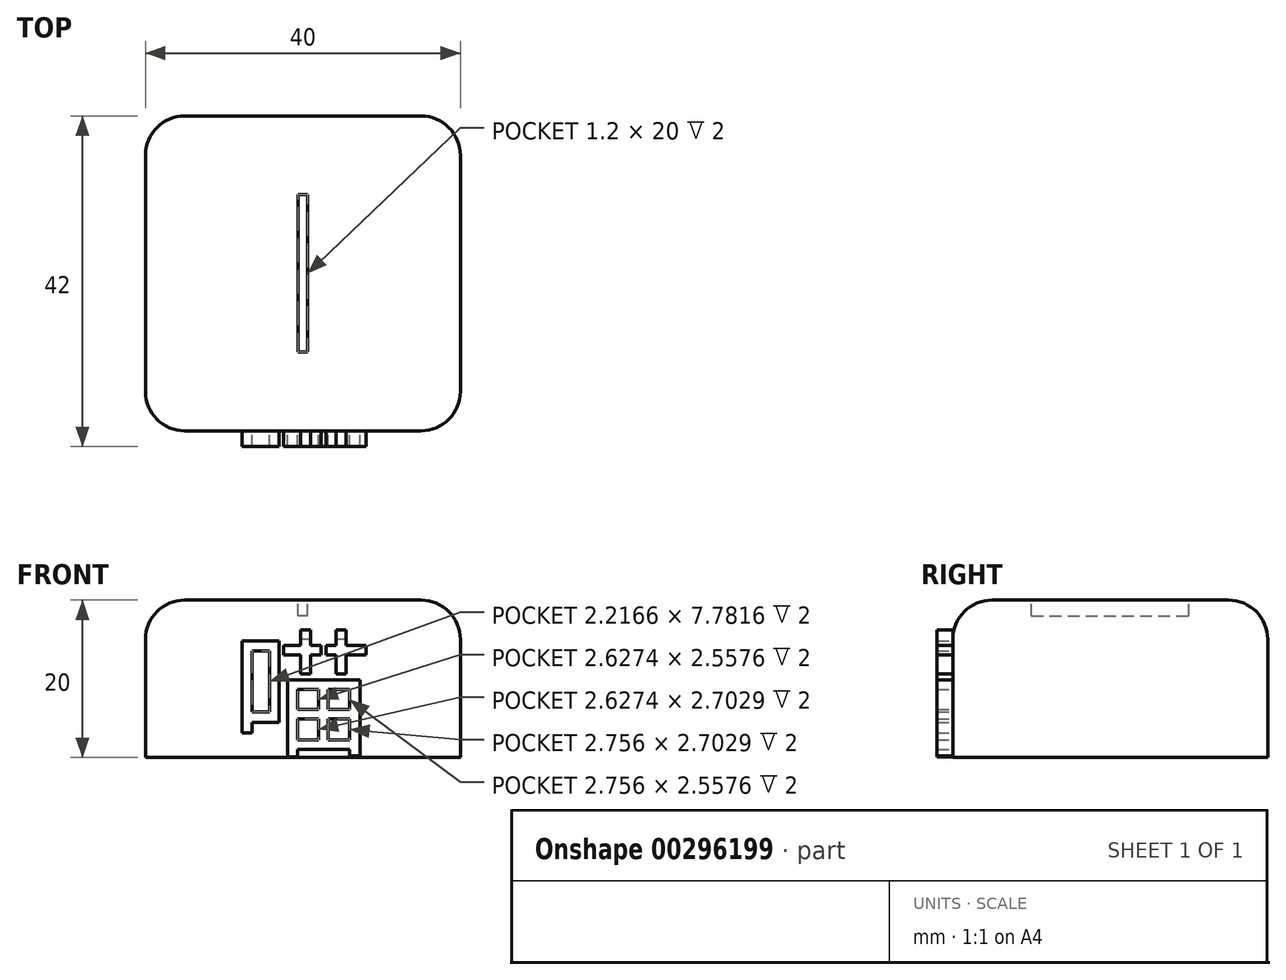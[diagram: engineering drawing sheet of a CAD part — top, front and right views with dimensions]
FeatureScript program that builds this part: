
annotation { "Feature Type Name" : "Feature", "Feature Type Description" : "" }
export const myFeature = defineFeature(function(context is Context, id is Id, definition is map)
    precondition{}
    {
        {
            var Q0;
            Q0=qCreatedBy(makeId("Top.planeOp"),FACE);
            var sketch = newSketch(context, id + "F0", { "sketchPlane" : qUnion([Q0])});
            skLineSegment(sketch, "E0.bottom", {"start": v(20, -20) * mm, "end": v(-20, -20) * mm});
            skLineSegment(sketch, "E0.top", {"start": v(20, 20) * mm, "end": v(-20, 20) * mm});
            skLineSegment(sketch, "E0.left", {"start": v(20, -20) * mm, "end": v(20, 20) * mm});
            skLineSegment(sketch, "E0.right", {"start": v(-20, -20) * mm, "end": v(-20, 20) * mm});
            skPoint(sketch, "E0.middle", {"position": v(0, 0) * mm});
            skLineSegment(sketch, "E1.bottom", {"start": v(0.6, -10) * mm, "end": v(-0.6, -10) * mm});
            skLineSegment(sketch, "E1.top", {"start": v(0.6, 10) * mm, "end": v(-0.6, 10) * mm});
            skLineSegment(sketch, "E1.left", {"start": v(0.6, -10) * mm, "end": v(0.6, 10) * mm});
            skLineSegment(sketch, "E1.right", {"start": v(-0.6, -10) * mm, "end": v(-0.6, 10) * mm});
            skSolve(sketch);
        }
        {
            var Q0;
            Q0=makeQuery(id+"F0.imprint","IMPRINT",FACE,{"disambiguationData":[TD([[makeQuery(id+"F0.imprint","IMPRINT",EDGE,{"derivedFrom":sQuery(id+"F0.wireOp",EDGE,"E0.bottom")}),-1.0]])]});
            var Q1;
            Q1=makeQuery(id+"F0.imprint","IMPRINT",FACE,{"disambiguationData":[TD([[makeQuery(id+"F0.imprint","IMPRINT",EDGE,{"derivedFrom":sQuery(id+"F0.wireOp",EDGE,"E1.bottom")}),-1.0]])]});
            extrude(context, id + "F1", {"entities" : qUnion([Q0, Q1]), "oppositeDirection" : true, "depth" : 20 * mm});
        }
        {
            var Q0;
            Q0=makeQuery(id+"F0.imprint","IMPRINT",FACE,{"disambiguationData":[TD([[makeQuery(id+"F0.imprint","IMPRINT",EDGE,{"derivedFrom":sQuery(id+"F0.wireOp",EDGE,"E1.bottom")}),-1.0]])]});
            extrude(context, id + "F2", {"entities" : qUnion([Q0]), "operationType" : NewBodyOperationType.REMOVE, "oppositeDirection" : true, "depth" : 2 * mm});
        }
        {
            var Q0;
            Q0=makeQuery(id+"F2.boolean.opBoolean","COPY",EDGE,{"derivedFrom":makeQuery(id+"F2.opExtrude","CAP_EDGE",EDGE,{"disambiguationData":[OSD([sQuery(id+"F0.wireOp",EDGE,"E1.left")])],"isStart":true})});
            var Q1;
            Q1=makeQuery(id+"F2.boolean.opBoolean","COPY",EDGE,{"derivedFrom":makeQuery(id+"F2.opExtrude","CAP_EDGE",EDGE,{"disambiguationData":[OSD([sQuery(id+"F0.wireOp",EDGE,"E1.right")])],"isStart":true})});
            var Q2;
            Q2=makeQuery(id+"F1.opExtrude","SWEPT_EDGE",EDGE,{"disambiguationData":[OSD([sQuery(id+"F0.wireOp",EDGE,"E0.bottom"),sQuery(id+"F0.wireOp",EDGE,"E0.left")])]});
            var Q3;
            Q3=makeQuery(id+"F1.opExtrude","SWEPT_EDGE",EDGE,{"disambiguationData":[OSD([sQuery(id+"F0.wireOp",EDGE,"E0.top"),sQuery(id+"F0.wireOp",EDGE,"E0.left")])]});
            var Q4;
            Q4=makeQuery(id+"F1.opExtrude","CAP_EDGE",EDGE,{"disambiguationData":[OSD([sQuery(id+"F0.wireOp",EDGE,"E0.left")])],"isStart":true});
            var Q5;
            Q5=makeQuery(id+"F1.opExtrude","SWEPT_EDGE",EDGE,{"disambiguationData":[OSD([sQuery(id+"F0.wireOp",EDGE,"E0.bottom"),sQuery(id+"F0.wireOp",EDGE,"E0.right")])]});
            var Q6;
            Q6=makeQuery(id+"F1.opExtrude","SWEPT_EDGE",EDGE,{"disambiguationData":[OSD([sQuery(id+"F0.wireOp",EDGE,"E0.top"),sQuery(id+"F0.wireOp",EDGE,"E0.right")])]});
            var Q7;
            Q7=makeQuery(id+"F1.opExtrude","CAP_EDGE",EDGE,{"disambiguationData":[OSD([sQuery(id+"F0.wireOp",EDGE,"E0.top")])],"isStart":true});
            var Q8;
            Q8=makeQuery(id+"F1.opExtrude","CAP_EDGE",EDGE,{"disambiguationData":[OSD([sQuery(id+"F0.wireOp",EDGE,"E0.right")])],"isStart":true});
            var Q9;
            Q9=makeQuery(id+"F1.opExtrude","CAP_EDGE",EDGE,{"disambiguationData":[OSD([sQuery(id+"F0.wireOp",EDGE,"E0.bottom")])],"isStart":true});
            fillet(context, id + "F3", {"entities" : qUnion([Q0, Q1, Q2, Q3, Q4, Q5, Q6, Q7, Q8, Q9]), "radius" : 5 * mm, "tangentPropagation" : true, "allowEdgeOverflow" : false});
        }
        {
            var Q0;
            Q0=makeQuery(id+"F1.opExtrude","SWEPT_FACE",FACE,{"disambiguationData":[OSD([sQuery(id+"F0.wireOp",EDGE,"E0.bottom")])]});
            var sketch = newSketch(context, id + "F4", { "sketchPlane" : qUnion([Q0])});
            skText(sketch, "E2", { "text": "喵", "fontName": "NotoSansCJKtc-Regular.otf"});
            const initialGuessF4  = {"E2": [-0.00905, -0.01851, 1, 0, 0.01288]};
            skSetInitialGuess(sketch, initialGuessF4);
            skSolve(sketch);
        }
        {
            var Q0;
            Q0=makeQuery(id+"F4.imprint","IMPRINT",FACE,{"disambiguationData":[TD([[makeQuery(id+"F4.imprint","IMPRINT",EDGE,{"derivedFrom":sQuery(id+"F4.wireOp",EDGE,"E2.sketch_text.stroke-22")}),1.0]])]});
            var Q1;
            Q1=makeQuery(id+"F4.imprint","IMPRINT",FACE,{"disambiguationData":[TD([[makeQuery(id+"F4.imprint","IMPRINT",EDGE,{"derivedFrom":sQuery(id+"F4.wireOp",EDGE,"E2.sketch_text.stroke-10")}),1.0]])]});
            var Q2;
            {var subQ5=sQuery(id+"F4.wireOp",EDGE,"E2.sketch_text.stroke-49");Q2=makeQuery(id+"F4.imprint","IMPRINT",FACE,{"disambiguationData":[TD([[makeQuery(id+"F4.imprint","IMPRINT",EDGE,{"derivedFrom":subQ5}),1.0]])]});}
            var Q3;
            {var subQ0=sQuery(id+"F4.wireOp",EDGE,"E2.sketch_text.stroke-47");Q3=makeQuery(id+"F4.imprint","IMPRINT",FACE,{"disambiguationData":[TD([[makeQuery(id+"F4.imprint","IMPRINT",EDGE,{"derivedFrom":subQ0}),1.0]])]});}
            var Q4;
            {var subQ0=sQuery(id+"F4.wireOp",EDGE,"E2.sketch_text.stroke-16");Q4=makeQuery(id+"F4.imprint","IMPRINT",FACE,{"disambiguationData":[TD([[makeQuery(id+"F4.imprint","IMPRINT",EDGE,{"derivedFrom":subQ0}),1.0]])]});}
            var Q5;
            Q5=makeQuery(id+"F4.imprint","IMPRINT",FACE,{"disambiguationData":[TD([[makeQuery(id+"F4.imprint","IMPRINT",EDGE,{"derivedFrom":sQuery(id+"F4.wireOp",EDGE,"E2.sketch_text.stroke-0")}),1.0]])]});
            extrude(context, id + "F5", {"entities" : qUnion([Q0, Q1, Q2, Q3, Q4, Q5]), "operationType" : NewBodyOperationType.ADD, "depth" : 2 * mm});
        }
    });
